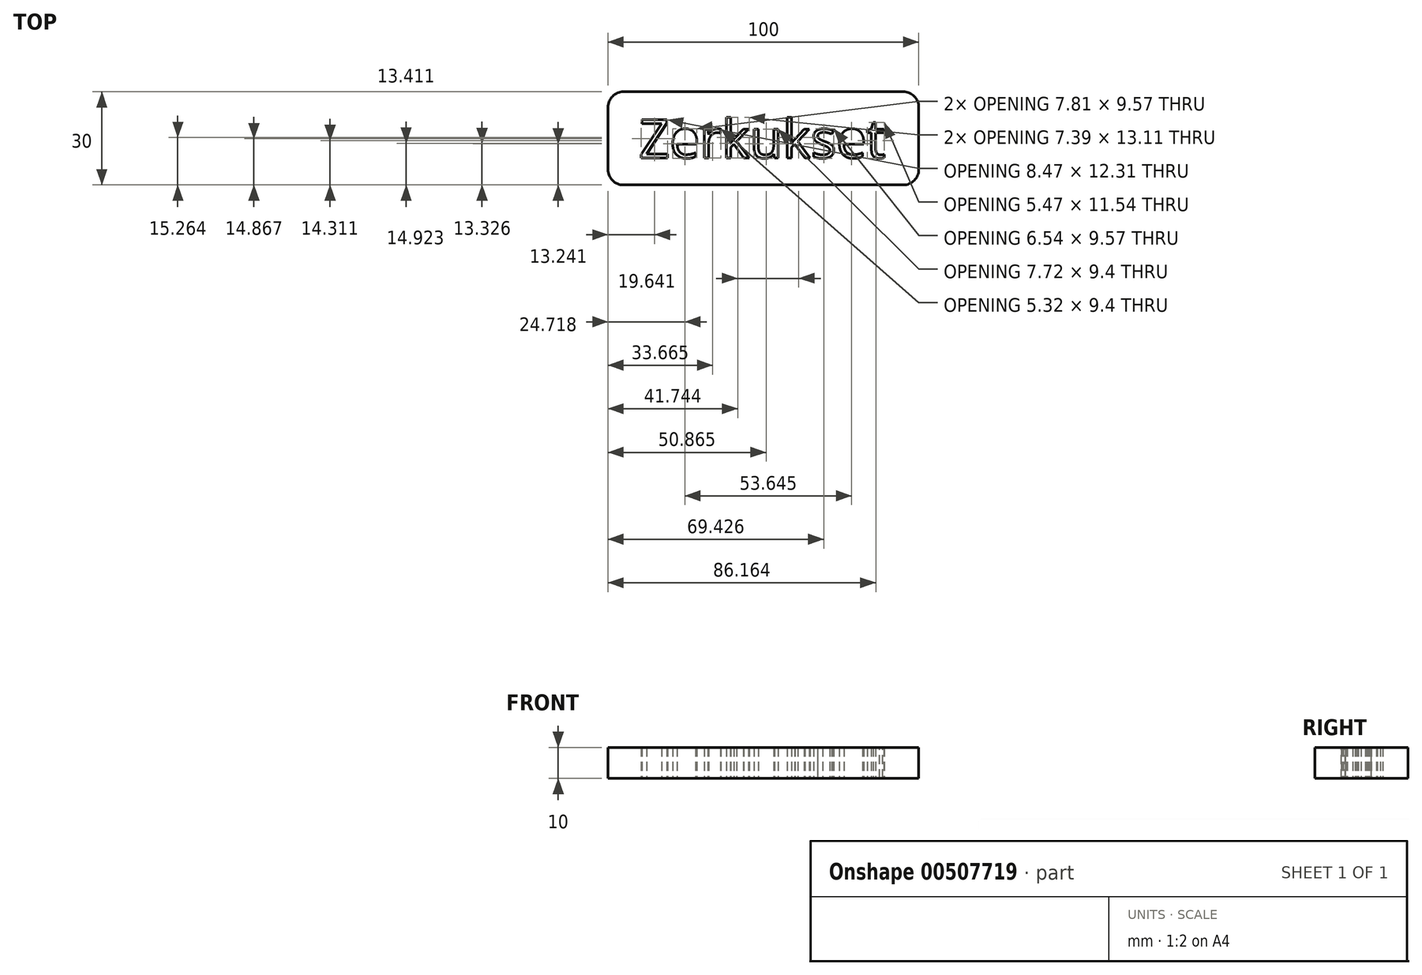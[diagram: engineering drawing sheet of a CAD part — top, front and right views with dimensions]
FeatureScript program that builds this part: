
annotation { "Feature Type Name" : "Feature", "Feature Type Description" : "" }
export const myFeature = defineFeature(function(context is Context, id is Id, definition is map)
    precondition{}
    {
        {
            var Q0;
            Q0=qCreatedBy(makeId("Top.planeOp"),FACE);
            var sketch = newSketch(context, id + "F0", { "sketchPlane" : qUnion([Q0])});
            skLineSegment(sketch, "E0.bottom", {"start": v(-48.22, 48.73) * mm, "end": v(51.78, 48.73) * mm});
            skLineSegment(sketch, "E0.top", {"start": v(-48.22, 18.73) * mm, "end": v(51.78, 18.73) * mm});
            skLineSegment(sketch, "E0.left", {"start": v(-48.22, 48.73) * mm, "end": v(-48.22, 18.73) * mm});
            skLineSegment(sketch, "E0.right", {"start": v(51.78, 48.73) * mm, "end": v(51.78, 18.73) * mm});
            skText(sketch, "E1", { "text": "Zerkukset\n", "fontName": "OpenSans-Regular.ttf"});
            const initialGuessF0  = {"E1": [-0.03822, 0.02744, 1, 0, 0.01242]};
            skSetInitialGuess(sketch, initialGuessF0);
            skSolve(sketch);
        }
        {
            var Q0;
            Q0 = qSketchRegion(id + "F0", true);
            extrude(context, id + "F1", {"entities" : qUnion([Q0]), "depth" : 10 * mm});
        }
        {
            var Q0;
            Q0=makeQuery(id+"F1.opExtrude","SWEPT_EDGE",EDGE,{"disambiguationData":[OSD([sQuery(id+"F0.wireOp",EDGE,"E0.top"),sQuery(id+"F0.wireOp",EDGE,"E0.right")])]});
            fillet(context, id + "F2", {"entities" : qUnion([Q0]), "radius" : 5 * mm, "tangentPropagation" : true, "allowEdgeOverflow" : false});
        }
        {
            var Q0;
            Q0=makeQuery(id+"F1.opExtrude","SWEPT_EDGE",EDGE,{"disambiguationData":[OSD([sQuery(id+"F0.wireOp",EDGE,"E0.bottom"),sQuery(id+"F0.wireOp",EDGE,"E0.right")])]});
            var Q1;
            Q1=makeQuery(id+"F1.opExtrude","SWEPT_EDGE",EDGE,{"disambiguationData":[OSD([sQuery(id+"F0.wireOp",EDGE,"E0.bottom"),sQuery(id+"F0.wireOp",EDGE,"E0.left")])]});
            var Q2;
            Q2=makeQuery(id+"F1.opExtrude","SWEPT_EDGE",EDGE,{"disambiguationData":[OSD([sQuery(id+"F0.wireOp",EDGE,"E0.top"),sQuery(id+"F0.wireOp",EDGE,"E0.left")])]});
            fillet(context, id + "F3", {"entities" : qUnion([Q0, Q1, Q2]), "radius" : 5 * mm, "tangentPropagation" : true, "allowEdgeOverflow" : false});
        }
    });
